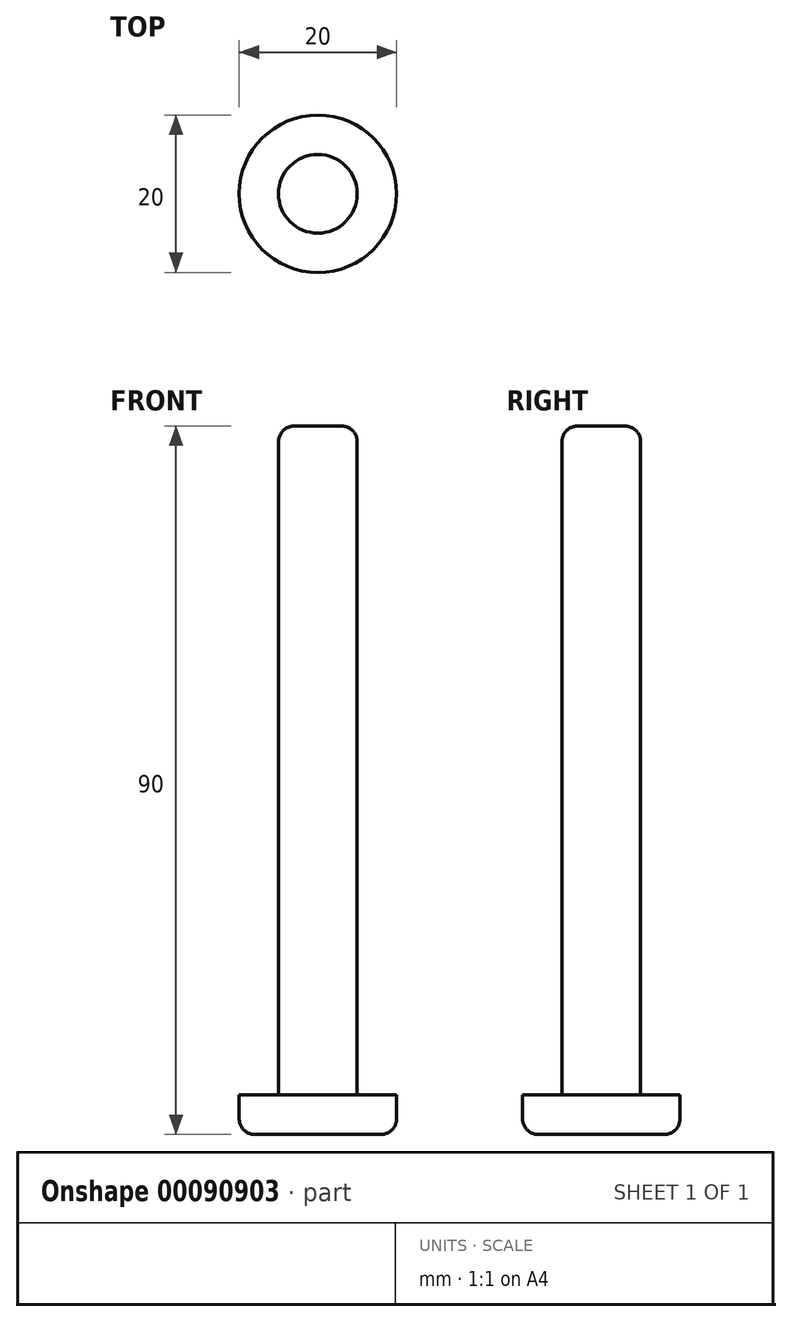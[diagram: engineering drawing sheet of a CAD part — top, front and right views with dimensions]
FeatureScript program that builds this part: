
annotation { "Feature Type Name" : "Feature", "Feature Type Description" : "" }
export const myFeature = defineFeature(function(context is Context, id is Id, definition is map)
    precondition{}
    {
        {
            var Q0;
            Q0=qCreatedBy(makeId("Top.planeOp"),FACE);
            var sketch = newSketch(context, id + "F0", { "sketchPlane" : qUnion([Q0])});
            skCircle(sketch, "E0", {"center": v(0, 0) * mm, "radius": 10 * mm});
            skSolve(sketch);
        }
        {
            var Q0;
            Q0 = qSketchRegion(id + "F0", true);
            var Q1;
            Q1=makeQuery(id+"F0.imprint","IMPRINT",FACE,{"disambiguationData":[TD([[makeQuery(id+"F0.imprint","IMPRINT",EDGE,{"derivedFrom":sQuery(id+"F0.wireOp",EDGE,"E0")}),1.0]])]});
            extrude(context, id + "F1", {"entities" : qUnion([Q0, Q1]), "depth" : 5 * mm});
        }
        {
            var Q0;
            Q0=makeQuery(id+"F1.opExtrude","CAP_FACE",FACE,{"disambiguationData":[OSD([sQuery(id+"F0.wireOp",EDGE,"E0")])],"isStart":false});
            var sketch = newSketch(context, id + "F2", { "sketchPlane" : qUnion([Q0])});
            skCircle(sketch, "E1", {"center": v(0, 0) * mm, "radius": 5 * mm});
            skSolve(sketch);
        }
        {
            var Q0;
            Q0 = qSketchRegion(id + "F2", true);
            var Q1;
            Q1=makeQuery(id+"F2.imprint","IMPRINT",FACE,{"disambiguationData":[TD([[makeQuery(id+"F2.imprint","IMPRINT",EDGE,{"derivedFrom":sQuery(id+"F2.wireOp",EDGE,"E1")}),1.0]])]});
            extrude(context, id + "F3", {"entities" : qUnion([Q0, Q1]), "operationType" : NewBodyOperationType.ADD, "depth" : 85 * mm});
        }
        {
            var Q0;
            Q0=makeQuery(id+"F3.opExtrude","CAP_EDGE",EDGE,{"disambiguationData":[OSD([sQuery(id+"F2.wireOp",EDGE,"E1")])],"isStart":false});
            var Q1;
            Q1=makeQuery(id+"F1.opExtrude","CAP_EDGE",EDGE,{"disambiguationData":[OSD([sQuery(id+"F0.wireOp",EDGE,"E0")])],"isStart":true});
            fillet(context, id + "F4", {"entities" : qUnion([Q0, Q1]), "radius" : 2 * mm, "tangentPropagation" : true, "allowEdgeOverflow" : false});
        }
    });
